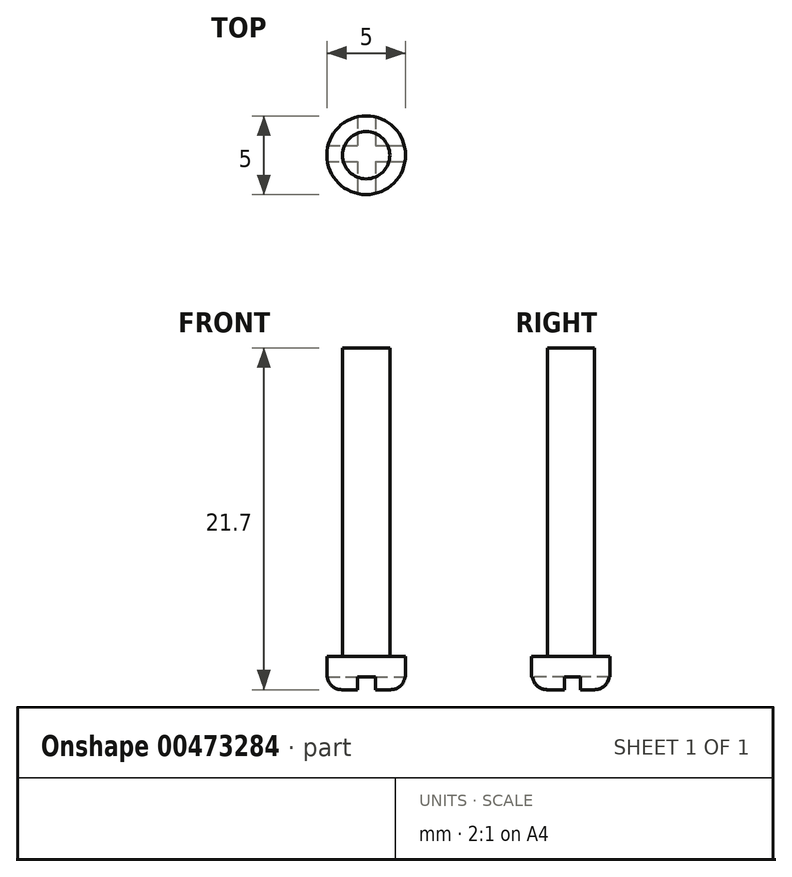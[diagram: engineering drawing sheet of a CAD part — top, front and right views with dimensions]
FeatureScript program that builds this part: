
annotation { "Feature Type Name" : "Feature", "Feature Type Description" : "" }
export const myFeature = defineFeature(function(context is Context, id is Id, definition is map)
    precondition{}
    {
        {
            var Q0;
            Q0=qCreatedBy(makeId("Top.planeOp"),FACE);
            var sketch = newSketch(context, id + "F0", { "sketchPlane" : qUnion([Q0])});
            skCircle(sketch, "E0", {"center": v(0, 0) * mm, "radius": 2.5 * mm});
            skSolve(sketch);
        }
        {
            var Q0;
            Q0 = qSketchRegion(id + "F0", true);
            extrude(context, id + "F1", {"entities" : qUnion([Q0]), "depth" : 2.1 * mm, "offsetDistance" : 25 * mm});
        }
        {
            var Q0;
            Q0=makeQuery(id+"F1.opExtrude","CAP_FACE",FACE,{"disambiguationData":[OSD([sQuery(id+"F0.wireOp",EDGE,"E0")])],"isStart":false});
            var sketch = newSketch(context, id + "F2", { "sketchPlane" : qUnion([Q0])});
            skCircle(sketch, "E1", {"center": v(0, 0) * mm, "radius": 1.5 * mm});
            skSolve(sketch);
        }
        {
            var Q0;
            Q0 = qSketchRegion(id + "F2", true);
            extrude(context, id + "F3", {"entities" : qUnion([Q0]), "operationType" : NewBodyOperationType.ADD, "depth" : 19.6 * mm, "offsetDistance" : 25 * mm});
        }
        {
            var Q0;
            Q0=makeQuery(id+"F1.opExtrude","CAP_EDGE",EDGE,{"disambiguationData":[OSD([sQuery(id+"F0.wireOp",EDGE,"E0")])],"isStart":true});
            fillet(context, id + "F4", {"entities" : qUnion([Q0]), "tangentPropagation" : true, "radius" : 0.9 * mm, "defaultsChanged" : true, "vertexSettings" : [], "allowEdgeOverflow" : false});
        }
        {
            var Q0;
            Q0=makeQuery(id+"F1.opExtrude","CAP_FACE",FACE,{"disambiguationData":[OSD([sQuery(id+"F0.wireOp",EDGE,"E0")])],"isStart":true});
            var sketch = newSketch(context, id + "F5", { "sketchPlane" : qUnion([Q0])});
            skLineSegment(sketch, "E2.bottom", {"start": v(-2.89, 0.4) * mm, "end": v(3.23, 0.4) * mm});
            skLineSegment(sketch, "E2.top", {"start": v(-2.89, -0.6) * mm, "end": v(3.23, -0.6) * mm});
            skLineSegment(sketch, "E2.left", {"start": v(-2.89, 0.4) * mm, "end": v(-2.89, -0.6) * mm});
            skLineSegment(sketch, "E2.right", {"start": v(3.23, 0.4) * mm, "end": v(3.23, -0.6) * mm});
            skLineSegment(sketch, "E3.bottom", {"start": v(-0.54, -2.57) * mm, "end": v(0.6, -2.57) * mm});
            skLineSegment(sketch, "E3.top", {"start": v(-0.54, 2.6) * mm, "end": v(0.6, 2.6) * mm});
            skLineSegment(sketch, "E3.left", {"start": v(-0.54, -2.57) * mm, "end": v(-0.54, 2.6) * mm});
            skLineSegment(sketch, "E3.right", {"start": v(0.6, -2.57) * mm, "end": v(0.6, 2.6) * mm});
            skSolve(sketch);
        }
        {
            var Q0;
            Q0 = qSketchRegion(id + "F5", true);
            extrude(context, id + "F6", {"entities" : qUnion([Q0]), "operationType" : NewBodyOperationType.REMOVE, "oppositeDirection" : true, "depth" : 0.8 * mm, "offsetDistance" : 25 * mm});
        }
    });
